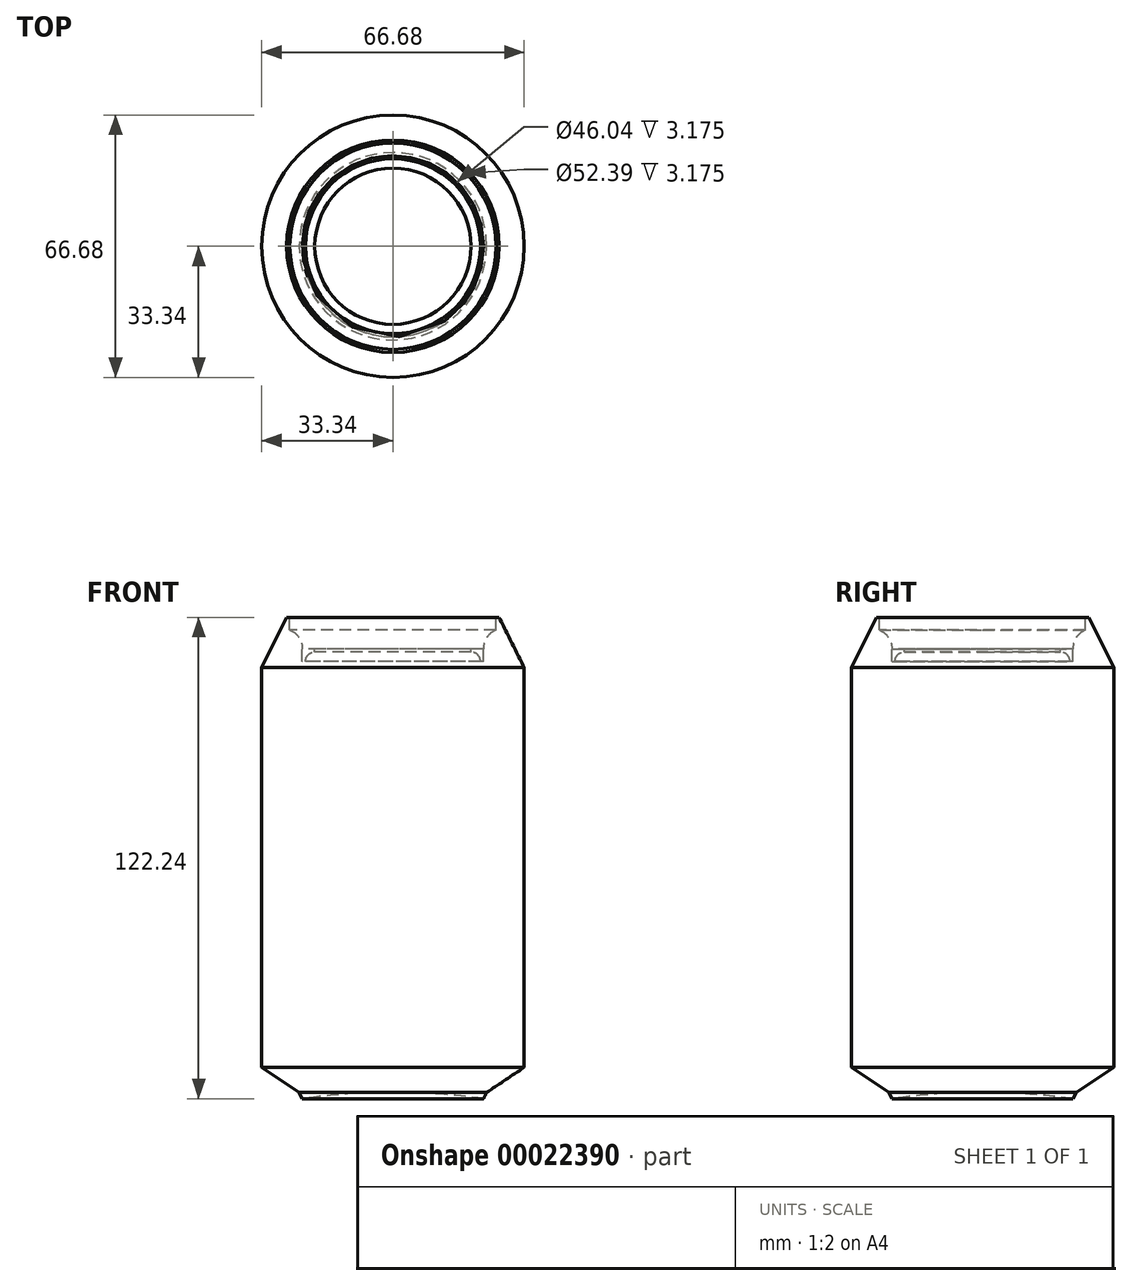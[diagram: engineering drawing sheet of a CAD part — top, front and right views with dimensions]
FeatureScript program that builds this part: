
annotation { "Feature Type Name" : "Feature", "Feature Type Description" : "" }
export const myFeature = defineFeature(function(context is Context, id is Id, definition is map)
    precondition{}
    {
        {
            var Q0;
            Q0=qCreatedBy(makeId("Right.planeOp"),FACE);
            var sketch = newSketch(context, id + "F0", { "sketchPlane" : qUnion([Q0])});
            skLineSegment(sketch, "E0", {"start": v(-33.34, 6.35) * mm, "end": v(-23.81, 0) * mm});
            skLineSegment(sketch, "E1", {"start": v(-33.34, 6.35) * mm, "end": v(-33.34, 107.95) * mm});
            skLineSegment(sketch, "E2", {"start": v(-33.34, 107.95) * mm, "end": v(-26.99, 120.65) * mm});
            skLineSegment(sketch, "E3", {"start": v(-26.99, 120.65) * mm, "end": v(-26.2, 120.65) * mm});
            skLineSegment(sketch, "E4", {"start": v(-26.2, 120.65) * mm, "end": v(-26.2, 117.47) * mm});
            skArc(sketch, "E5", {"start": v(-23.02, 112.71) * mm, "mid": v(-23.87, 115.59) * mm, "end": v(-26.2, 117.47) * mm});
            skLineSegment(sketch, "E6", {"start": v(-23.02, 112.71) * mm, "end": v(-23.02, 109.54) * mm});
            skLineSegment(sketch, "E7", {"start": v(-23.02, 109.54) * mm, "end": v(-22.23, 109.54) * mm});
            skArc(sketch, "E8", {"start": v(-19.84, 111.92) * mm, "mid": v(-21.5, 111.2) * mm, "end": v(-22.23, 109.54) * mm});
            skLineSegment(sketch, "E9", {"start": v(-19.84, 112.71) * mm, "end": v(-19.84, 111.92) * mm});
            skLineSegment(sketch, "E10", {"start": v(-23.81, 0) * mm, "end": v(-23.02, -1.59) * mm});
            skArc(sketch, "E11", {"start": v(23.02, -1.59) * mm, "mid": v(0, 0) * mm, "end": v(-23.02, -1.59) * mm});
            skLineSegment(sketch, "E12", {"start": v(-19.84, 112.71) * mm, "end": v(0, 112.71) * mm});
            skLineSegment(sketch, "E13", {"start": v(0, 112.71) * mm, "end": v(0, 0) * mm});
            skSolve(sketch);
        }
        {
            var Q0;
            Q0=makeQuery(id+"F0.imprint","IMPRINT",FACE,{"disambiguationData":[TD([[makeQuery(id+"F0.imprint","IMPRINT",EDGE,{"derivedFrom":sQuery(id+"F0.wireOp",EDGE,"E0")}),1.0]])]});
            var Q1;
            Q1=sQuery(id+"F0.wireOp",EDGE,"E13");
            revolve(context, id + "F1", {"entities" : qUnion([Q0]), "axis" : qUnion([Q1]), "revolveType" : RevolveType.FULL});
        }
    });
